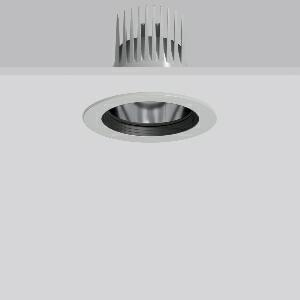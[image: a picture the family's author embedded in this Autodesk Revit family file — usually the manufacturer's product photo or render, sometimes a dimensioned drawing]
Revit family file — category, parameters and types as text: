
# Revit family: heledon_maxi_e_901759_004_2_76_4242
name_source: partatom
category: Lighting Fixtures
units: mm (PartAtom-declared; Revit-internal decimal feet)

## family parameters
Cut with Voids When Loaded = No
Host = Face
Light Source = No
Part Type = Normal
Room Calculation Point = No
Round Connector Dimension = Use Diameter
Shared = No

## types (1)
- HELEDON maxi E (1 x LED Modul 927, 3050 lm, 2700)
    Apparent Load = 25 VA
    Approval mark = CE
    CIE Flux Codes = 97 100 100 100 100
    Color Rendering = 92
    Color Temperature = 2700
    Default Elevation = 1800 mm
    Description = Series: HELEDON maxi
Round recessed downlight. Housing: die-cast aluminium, powder-coated. Black plastic ring and recessed LED to prevent glare from the side. Optical assembly with reflector made of MIRO-Silver with 98% total light reflection for outstanding efficiency - can be changed without tools. Best colour rendering index Ra>90. Suitable for Recessed ceiling mounting. Installation without tools thanks to spring fastening system. Including separate LED converter with connecting cable 600 mm.High quality converter without flickering and stroboscopic effect. Through-wiring box (5 pole) available as accessory. The following accessories can be mounted without use of tools: interchangeable lenses, decorative glasses, honeycomb louvre, clear and frosted diffusers, white interchangeable plastic ring. 
Colour: silver
Diameter: 162 mm
Height: 3 mm
Cut-out diameter: 152 mm
Recess height: 200 mm
Luminaire: recess height: 135 mm
Lamp: LED
Socket: without socket
Colour temperature: 2700K
Colour rendering index (CRI): 92
System power: 25 W
Rated luminous flux: 3050 lm
Luminous efficiency: 122 lm/W
Control gear: Converter, dimmable, DALI
Protection class: II
Type of protection: IP 20
    Height = 0 mm  [stored 0 ft]
    Lamp = 1 x LED Modul 927
    Lamp Light Flux = 3050 lm
    Lamp count = 1
    Length = 162 mm
    Lifetime = 50000 h
    Luminous efficacy = 122 lm/W
    Manufacturer = RZB
    ModVariant = No
    Model = 901759.004.2.76
    Mounting Place = Ceiling
    Mounting Type = Recessed
    Number of Poles = 1
    OnlyDefault = Yes
    Power Factor = 1
    Product Name = HELEDON maxi E
    Product group = Recessed downlights
    ProductGroupID = 402
    Protection Class = Protection class II
    Protection Degree = IP 20
    RLX_Detail_Level = 1
    RLX_Emergency_Light_Flux = 0 lm
    RLX_Emergency_Type = 0
    RLX_Emergency_Type_DB = No
    RlxData = <blob elided: 120297 chars, md5=c15fdd8a>
    Socket = socket
    Standby Power = 0 W
    System Light Flux = 3050 lm
    System Power = 25 W
    Type Comments = Product without accessories
    Type Image = 901662.004.jpg
    URL = http://relux.com
    VarID = ---
    Voltage = 230 V
    Voltage Range = 220-240 V
    Weight = 0.00 kg
    Width = 0 mm  [stored 0 ft]

note: [stored X ft] marks values corroborated as IEEE doubles in the binary element streams (Revit-internal decimal feet)

## geometry (parser evidence)
native form markers: Blend x4, Sweep x11
no freeform markers — native parametric forms only
